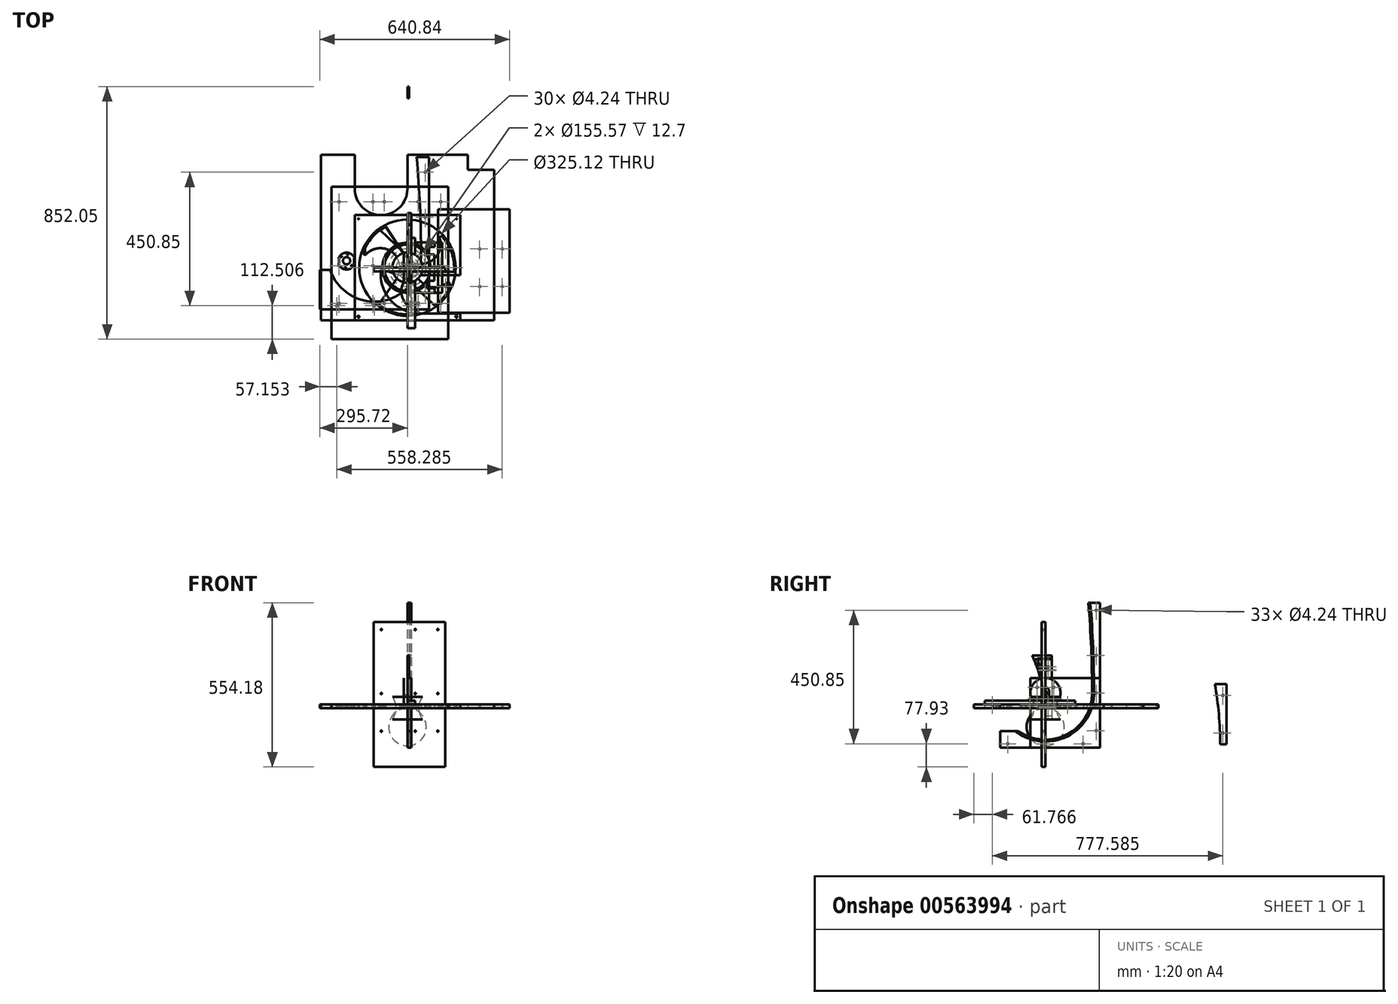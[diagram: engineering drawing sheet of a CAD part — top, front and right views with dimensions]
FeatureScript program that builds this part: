
annotation { "Feature Type Name" : "Feature", "Feature Type Description" : "" }
export const myFeature = defineFeature(function(context is Context, id is Id, definition is map)
    precondition{}
    {
        {
            var Q0;
            Q0=qCreatedBy(makeId("Front.planeOp"),FACE);
            var sketch = newSketch(context, id + "F0", { "sketchPlane" : qUnion([Q0])});
            skArc(sketch, "E0", {"start": v(50.8, 38.1) * mm, "mid": v(38.1, 0) * mm, "end": v(50.8, -38.1) * mm});
            skLineSegment(sketch, "E1.bottom", {"start": v(0, 38.1) * mm, "end": v(50.8, 38.1) * mm});
            skLineSegment(sketch, "E1.top", {"start": v(0, -38.1) * mm, "end": v(50.8, -38.1) * mm});
            skLineSegment(sketch, "E1.left", {"start": v(0, 38.1) * mm, "end": v(0, -38.1) * mm});
            skSolve(sketch);
        }
        {
            var Q0;
            Q0=qSketchRegion(id+"F0",true);
            var Q1;
            Q1=sQuery(id+"F0.wireOp",EDGE,"E1.left");
            revolve(context, id + "F1", {"entities" : qUnion([Q0]), "axis" : qUnion([Q1]), "revolveType" : RevolveType.FULL});
        }
        {
            var Q0;
            Q0=qCreatedBy(makeId("Right.planeOp"),FACE);
            var sketch = newSketch(context, id + "F2", { "sketchPlane" : qUnion([Q0])});
            skCircle(sketch, "E2", {"center": v(0, 50.8) * mm, "radius": 50.8 * mm});
            skCircle(sketch, "E3", {"center": v(0, 50.8) * mm, "radius": 6.35 * mm});
            skSolve(sketch);
        }
        {
            var Q0;
            Q0=qSketchRegion(id+"F2",true);
            extrude(context, id + "F3", {"entities" : qUnion([Q0]), "depth" : 25.4 * mm, "symmetric" : true});
        }
        {
            var Q0;
            Q0=qCreatedBy(makeId("Front.planeOp"),FACE);
            var sketch = newSketch(context, id + "F4", { "sketchPlane" : qUnion([Q0])});
            skArc(sketch, "E4", {"start": v(0, -127) * mm, "mid": v(63.5, -63.5) * mm, "end": v(0, 0) * mm});
            skLineSegment(sketch, "E5", {"start": v(0, 0) * mm, "end": v(0, -127) * mm});
            skSolve(sketch);
        }
        {
            var Q0;
            Q0=qSketchRegion(id+"F4",true);
            var Q1;
            Q1=sQuery(id+"F4.wireOp",EDGE,"E5");
            revolve(context, id + "F5", {"entities" : qUnion([Q0]), "axis" : qUnion([Q1]), "revolveType" : RevolveType.FULL});
        }
        {
            var Q0;
            Q0=qCreatedBy(makeId("Right.planeOp"),FACE);
            var sketch = newSketch(context, id + "F6", { "sketchPlane" : qUnion([Q0])});
            skLineSegment(sketch, "E6.top", {"start": v(-152.4, -133.35) * mm, "end": v(184.15, -133.35) * mm});
            skLineSegment(sketch, "E6.right", {"start": v(184.15, 50.8) * mm, "end": v(184.15, -133.35) * mm});
            skArc(sketch, "E7", {"start": v(-91.77, -77.18) * mm, "mid": v(71.93, -89.3) * mm, "end": v(157.48, 50.8) * mm});
            skLineSegment(sketch, "E8.left", {"start": v(184.15, 50.8) * mm, "end": v(184.15, 355.6) * mm});
            skArc(sketch, "E9", {"start": v(157.48, 50.8) * mm, "mid": v(154.4, 203.32) * mm, "end": v(145.19, 355.6) * mm});
            skCircle(sketch, "E10", {"center": v(-127, -120.65) * mm, "radius": 2.12 * mm});
            skCircle(sketch, "E11", {"center": v(0, -120.62) * mm, "radius": 2.12 * mm});
            skCircle(sketch, "E12", {"center": v(127, -120.62) * mm, "radius": 2.12 * mm});
            skCircle(sketch, "E13", {"center": v(171.45, 50.8) * mm, "radius": 2.12 * mm});
            skCircle(sketch, "E14", {"center": v(171.45, -76.2) * mm, "radius": 2.12 * mm});
            skCircle(sketch, "E15", {"center": v(171.45, 177.8) * mm, "radius": 2.12 * mm});
            skCircle(sketch, "E16", {"center": v(171.45, 330.2) * mm, "radius": 2.12 * mm});
            skLineSegment(sketch, "E17", {"start": v(-152.4, -77.18) * mm, "end": v(-91.77, -77.18) * mm});
            skLineSegment(sketch, "E18", {"start": v(-152.4, -77.18) * mm, "end": v(-152.4, -133.35) * mm});
            skPoint(sketch, "E19.orphan", {"position": v(-184.15, 0) * mm});
            skPoint(sketch, "E6.left.start.orphan", {"position": v(-184.15, -77.18) * mm});
            skPoint(sketch, "E20.orphan", {"position": v(-184.15, -133.35) * mm});
            skLineSegment(sketch, "E21", {"start": v(184.15, 355.6) * mm, "end": v(145.19, 355.6) * mm});
            skPoint(sketch, "E22.orphan", {"position": v(184.15, 381) * mm});
            skSolve(sketch);
        }
        {
            var Q0;
            Q0=qSketchRegion(id+"F6",true);
            extrude(context, id + "F7", {"entities" : qUnion([Q0]), "depth" : 12.7 * mm});
        }
        {
            var Q0;
            Q0=makeQuery(id+"F7.opExtrude","CAP_EDGE",EDGE,{"disambiguationData":[OSD([sQuery(id+"F6.wireOp",EDGE,"E9")])],"isStart":true});
            chamfer(context, id + "F8", {"entities" : qUnion([Q0]), "chamferType" : ChamferType.TWO_OFFSETS, "width1" : 3.66 * mm, "oppositeDirection" : false, "width2" : 6.35 * mm, "tangentPropagation" : true});
        }
        {
            var Q0;
            Q0=qCreatedBy(makeId("Top.planeOp"),FACE);
            var sketch = newSketch(context, id + "F9", { "sketchPlane" : qUnion([Q0])});
            skLineSegment(sketch, "E23.bottom", {"start": v(103.82, 196.85) * mm, "end": v(345.12, 196.85) * mm});
            skLineSegment(sketch, "E23.right", {"start": v(345.12, 196.85) * mm, "end": v(345.12, -152.4) * mm});
            skCircle(sketch, "E24", {"center": v(129.22, 63.5) * mm, "radius": 2.12 * mm});
            skCircle(sketch, "E25", {"center": v(129.22, -63.5) * mm, "radius": 2.12 * mm});
            skCircle(sketch, "E26", {"center": v(243.52, 63.5) * mm, "radius": 2.12 * mm});
            skCircle(sketch, "E27", {"center": v(243.52, -63.5) * mm, "radius": 2.12 * mm});
            skCircle(sketch, "E28", {"center": v(319.72, 63.5) * mm, "radius": 2.12 * mm});
            skCircle(sketch, "E29", {"center": v(319.72, -63.5) * mm, "radius": 2.12 * mm});
            skLineSegment(sketch, "E30", {"start": v(103.82, -152.4) * mm, "end": v(103.82, 196.85) * mm});
            skPoint(sketch, "E31.orphan", {"position": v(-48.58, 196.85) * mm});
            skPoint(sketch, "E32.center.orphan", {"position": v(-23.18, 63.5) * mm});
            skPoint(sketch, "E33.center.orphan", {"position": v(91.12, 63.5) * mm});
            skPoint(sketch, "E34.center.orphan", {"position": v(-23.18, -63.5) * mm});
            skPoint(sketch, "E35.center.orphan", {"position": v(91.12, -63.5) * mm});
            skLineSegment(sketch, "E36", {"start": v(103.82, -152.4) * mm, "end": v(345.12, -152.4) * mm});
            skPoint(sketch, "E23.top.start.orphan", {"position": v(103.82, -184.15) * mm});
            skSolve(sketch);
        }
        {
            var Q0;
            Q0=qSketchRegion(id+"F9",true);
            extrude(context, id + "F10", {"entities" : qUnion([Q0]), "depth" : 12.7 * mm});
        }
        {
            var Q0;
            Q0=qCreatedBy(makeId("Right.planeOp"),FACE);
            var sketch = newSketch(context, id + "F11", { "sketchPlane" : qUnion([Q0])});
            skLineSegment(sketch, "E37.bottom", {"start": v(-204.62, 25.4) * mm, "end": v(100.18, 25.4) * mm});
            skLineSegment(sketch, "E37.top", {"start": v(-204.62, 0) * mm, "end": v(100.18, 0) * mm});
            skLineSegment(sketch, "E37.left", {"start": v(-204.62, 25.4) * mm, "end": v(-204.62, 0) * mm});
            skLineSegment(sketch, "E37.right", {"start": v(100.18, 25.4) * mm, "end": v(100.18, 0) * mm});
            skCircle(sketch, "E38", {"center": v(-179.22, 12.7) * mm, "radius": 2.12 * mm});
            skCircle(sketch, "E39", {"center": v(-52.22, 12.7) * mm, "radius": 2.12 * mm});
            skCircle(sketch, "E40", {"center": v(74.78, 12.7) * mm, "radius": 2.12 * mm});
            skSolve(sketch);
        }
        {
            var Q0;
            Q0=qSketchRegion(id+"F11",true);
            extrude(context, id + "F12", {"entities" : qUnion([Q0]), "depth" : 25.4 * mm});
        }
        {
            var Q0;
            Q0=qCreatedBy(makeId("Top.planeOp"),FACE);
            var sketch = newSketch(context, id + "F13", { "sketchPlane" : qUnion([Q0])});
            skCircle(sketch, "E41", {"center": v(12.7, -115.72) * mm, "radius": 2.12 * mm});
            skCircle(sketch, "E42", {"center": v(12.7, 11.28) * mm, "radius": 2.12 * mm});
            skSolve(sketch);
        }
        {
            var Q0;
            Q0=sQuery(id+"F13.wireOp",VERTEX,"E41.center");
            var Q1;
            Q1=makeQuery(id+"F12.opExtrude","SWEPT_BODY",BODY,{"disambiguationData":[OSD([sQuery(id+"F11.wireOp",EDGE,"E37.bottom"),sQuery(id+"F11.wireOp",EDGE,"E37.top"),sQuery(id+"F11.wireOp",EDGE,"E37.left"),sQuery(id+"F11.wireOp",EDGE,"E37.right"),sQuery(id+"F11.wireOp",EDGE,"E38"),sQuery(id+"F11.wireOp",EDGE,"E39"),sQuery(id+"F11.wireOp",EDGE,"E40")])]});
            hole(context, id + "F14", {"style" : HoleStyle.SIMPLE, "endStyle" : HoleEndStyle.THROUGH, "oppositeDirection" : true, "holeDiameter" : 4.24 * mm, "isTappedThrough" : true, "tappedDepth" : 12.7 * mm, "tapClearance" : 3, "locations" : qUnion([Q0]), "scope" : qUnion([Q1]), "startStyle" : HoleStartStyle.PART});
        }
        {
            var Q0;
            Q0=sQuery(id+"F13.wireOp",VERTEX,"E42.center");
            var Q1;
            Q1=makeQuery(id+"F12.opExtrude","SWEPT_BODY",BODY,{"disambiguationData":[OSD([sQuery(id+"F11.wireOp",EDGE,"E37.bottom"),sQuery(id+"F11.wireOp",EDGE,"E37.top"),sQuery(id+"F11.wireOp",EDGE,"E37.left"),sQuery(id+"F11.wireOp",EDGE,"E37.right"),sQuery(id+"F11.wireOp",EDGE,"E38"),sQuery(id+"F11.wireOp",EDGE,"E39"),sQuery(id+"F11.wireOp",EDGE,"E40")])]});
            hole(context, id + "F15", {"style" : HoleStyle.SIMPLE, "endStyle" : HoleEndStyle.THROUGH, "oppositeDirection" : true, "holeDiameter" : 4.24 * mm, "isTappedThrough" : true, "tappedDepth" : 12.7 * mm, "tapClearance" : 3, "locations" : qUnion([Q0]), "scope" : qUnion([Q1]), "startStyle" : HoleStartStyle.PART});
        }
        {
            var Q0;
            Q0=qCreatedBy(makeId("Front.planeOp"),FACE);
            var sketch = newSketch(context, id + "F16", { "sketchPlane" : qUnion([Q0])});
            skLineSegment(sketch, "E43.top", {"start": v(-113.71, -198.58) * mm, "end": v(127.59, -198.58) * mm});
            skLineSegment(sketch, "E43.right", {"start": v(127.59, 290.37) * mm, "end": v(127.59, -198.58) * mm});
            skCircle(sketch, "E44", {"center": v(-88.31, 49.07) * mm, "radius": 2.12 * mm});
            skCircle(sketch, "E45", {"center": v(-88.31, -77.93) * mm, "radius": 2.12 * mm});
            skCircle(sketch, "E46", {"center": v(25.99, 49.07) * mm, "radius": 2.12 * mm});
            skCircle(sketch, "E47", {"center": v(25.99, -77.93) * mm, "radius": 2.12 * mm});
            skCircle(sketch, "E48", {"center": v(102.19, 49.07) * mm, "radius": 2.12 * mm});
            skCircle(sketch, "E49", {"center": v(102.19, -77.93) * mm, "radius": 2.12 * mm});
            skCircle(sketch, "E50", {"center": v(-88.31, 264.97) * mm, "radius": 2.12 * mm});
            skCircle(sketch, "E51", {"center": v(25.99, 264.97) * mm, "radius": 2.12 * mm});
            skCircle(sketch, "E52", {"center": v(102.19, 264.97) * mm, "radius": 2.12 * mm});
            skLineSegment(sketch, "E53", {"start": v(-113.71, 290.37) * mm, "end": v(-113.71, -198.58) * mm});
            skPoint(sketch, "E43.left.start.orphan", {"position": v(-266.11, 315.77) * mm});
            skPoint(sketch, "E54.center.orphan", {"position": v(-240.71, -77.93) * mm});
            skPoint(sketch, "E55.center.orphan", {"position": v(-126.41, -77.93) * mm});
            skPoint(sketch, "E56.center.orphan", {"position": v(-126.41, 49.07) * mm});
            skPoint(sketch, "E57.center.orphan", {"position": v(-240.71, 49.07) * mm});
            skPoint(sketch, "E58.center.orphan", {"position": v(-240.71, 264.97) * mm});
            skPoint(sketch, "E59.center.orphan", {"position": v(-126.41, 264.97) * mm});
            skLineSegment(sketch, "E60", {"start": v(-113.71, 290.37) * mm, "end": v(127.59, 290.37) * mm});
            skPoint(sketch, "E43.bottom.start.orphan", {"position": v(-113.71, 315.77) * mm});
            skSolve(sketch);
        }
        {
            var Q0;
            Q0=qSketchRegion(id+"F16",true);
            extrude(context, id + "F17", {"entities" : qUnion([Q0]), "depth" : 12.7 * mm});
        }
        {
            var Q0;
            Q0=qCreatedBy(makeId("Right.planeOp"),FACE);
            var sketch = newSketch(context, id + "F18", { "sketchPlane" : qUnion([Q0])});
            skLineSegment(sketch, "E61.bottom", {"start": v(184.15, -133.35) * mm, "end": v(-50.8, -133.35) * mm});
            skLineSegment(sketch, "E61.top", {"start": v(184.15, 101.6) * mm, "end": v(-50.8, 101.6) * mm});
            skLineSegment(sketch, "E61.left", {"start": v(184.15, -133.35) * mm, "end": v(184.15, 101.6) * mm});
            skLineSegment(sketch, "E61.right", {"start": v(-50.8, -133.35) * mm, "end": v(-50.8, 101.6) * mm});
            skCircle(sketch, "E62", {"center": v(171.45, 50.8) * mm, "radius": 2.12 * mm});
            skCircle(sketch, "E63", {"center": v(171.45, -76.2) * mm, "radius": 2.12 * mm});
            skCircle(sketch, "E64", {"center": v(127, -120.62) * mm, "radius": 2.12 * mm});
            skCircle(sketch, "E65", {"center": v(0, -120.62) * mm, "radius": 2.12 * mm});
            skArc(sketch, "E66", {"start": v(12.7, 57.15) * mm, "mid": v(0, 69.85) * mm, "end": v(-12.7, 57.15) * mm});
            skArc(sketch, "E67", {"start": v(-12.7, 44.45) * mm, "mid": v(0, 31.75) * mm, "end": v(12.7, 44.45) * mm});
            skLineSegment(sketch, "E68", {"start": v(-12.7, 44.45) * mm, "end": v(-12.7, 57.15) * mm});
            skLineSegment(sketch, "E69", {"start": v(12.7, 57.15) * mm, "end": v(12.7, 44.45) * mm});
            skCircle(sketch, "E70", {"center": v(27.94, 69.85) * mm, "radius": 2.12 * mm});
            skPoint(sketch, "E70.centerSnap0", {"position": v(0, 69.85) * mm});
            skCircle(sketch, "E71", {"center": v(-27.94, 69.85) * mm, "radius": 2.12 * mm});
            skCircle(sketch, "E72", {"center": v(27.94, 31.75) * mm, "radius": 2.12 * mm});
            skPoint(sketch, "E72.centerSnap0", {"position": v(0, 31.75) * mm});
            skCircle(sketch, "E73", {"center": v(-27.94, 31.75) * mm, "radius": 2.12 * mm});
            skSolve(sketch);
        }
        {
            var Q0;
            Q0=qSketchRegion(id+"F18",true);
            extrude(context, id + "F19", {"entities" : qUnion([Q0]), "depth" : 12.7 * mm});
        }
        {
            var Q0;
            Q0=qSketchRegion(id+"F6",true);
            extrude(context, id + "F20", {"entities" : qUnion([Q0]), "depth" : 12.7 * mm});
        }
        {
            var Q0;
            Q0=makeQuery(id+"F20.opExtrude","CAP_EDGE",EDGE,{"disambiguationData":[OSD([sQuery(id+"F6.wireOp",EDGE,"E9")])],"isStart":false});
            chamfer(context, id + "F21", {"entities" : qUnion([Q0]), "chamferType" : ChamferType.TWO_OFFSETS, "width1" : 6.35 * mm, "oppositeDirection" : false, "width2" : 3.66 * mm, "tangentPropagation" : true});
        }
        {
            var Q0;
            Q0=qCreatedBy(makeId("Top.planeOp"),FACE);
            var sketch = newSketch(context, id + "F22", { "sketchPlane" : qUnion([Q0])});
            skLineSegment(sketch, "E74.top", {"start": v(-295.72, -141.18) * mm, "end": v(72.58, -141.18) * mm});
            skLineSegment(sketch, "E74.left", {"start": v(-295.72, -7.83) * mm, "end": v(-295.72, -141.18) * mm});
            skLineSegment(sketch, "E74.right", {"start": v(72.58, 42.97) * mm, "end": v(72.58, -141.18) * mm});
            skArc(sketch, "E75", {"start": v(-260.63, -7.83) * mm, "mid": v(-85.82, -112.4) * mm, "end": v(45.91, 42.97) * mm});
            skLineSegment(sketch, "E76.top", {"start": v(72.58, 373.17) * mm, "end": v(31.48, 373.17) * mm});
            skLineSegment(sketch, "E76.left", {"start": v(72.58, 42.97) * mm, "end": v(72.58, 373.17) * mm});
            skArc(sketch, "E77", {"start": v(45.91, 42.97) * mm, "mid": v(42.3, 208.22) * mm, "end": v(31.48, 373.17) * mm});
            skCircle(sketch, "E78", {"center": v(-238.57, -128.48) * mm, "radius": 2.12 * mm});
            skCircle(sketch, "E79", {"center": v(-111.57, -128.46) * mm, "radius": 2.12 * mm});
            skCircle(sketch, "E80", {"center": v(15.43, -128.46) * mm, "radius": 2.12 * mm});
            skCircle(sketch, "E81", {"center": v(59.88, 42.97) * mm, "radius": 2.12 * mm});
            skCircle(sketch, "E82", {"center": v(59.88, -84.03) * mm, "radius": 2.12 * mm});
            skCircle(sketch, "E83", {"center": v(59.88, 169.97) * mm, "radius": 2.12 * mm});
            skCircle(sketch, "E84", {"center": v(59.88, 322.37) * mm, "radius": 2.12 * mm});
            skLineSegment(sketch, "E85", {"start": v(-295.72, -7.83) * mm, "end": v(-260.63, -7.83) * mm});
            skSolve(sketch);
        }
        {
            var Q0;
            Q0=qSketchRegion(id+"F22",true);
            extrude(context, id + "F23", {"entities" : qUnion([Q0]), "depth" : 12.7 * mm});
        }
        {
            var Q0;
            Q0=qCreatedBy(makeId("Top.planeOp"),FACE);
            var sketch = newSketch(context, id + "F24", { "sketchPlane" : qUnion([Q0])});
            skLineSegment(sketch, "E86.bottom", {"start": v(-256.02, 273.36) * mm, "end": v(137.68, 273.36) * mm});
            skLineSegment(sketch, "E86.top", {"start": v(-256.02, -241) * mm, "end": v(137.68, -241) * mm});
            skLineSegment(sketch, "E86.left", {"start": v(-256.02, 273.36) * mm, "end": v(-256.02, -241) * mm});
            skLineSegment(sketch, "E86.right", {"start": v(137.68, 273.36) * mm, "end": v(137.68, -241) * mm});
            skCircle(sketch, "E87", {"center": v(-230.62, -120.34) * mm, "radius": 2.12 * mm});
            skCircle(sketch, "E88", {"center": v(-230.62, 6.66) * mm, "radius": 2.12 * mm});
            skCircle(sketch, "E89", {"center": v(-116.32, 6.66) * mm, "radius": 2.12 * mm});
            skCircle(sketch, "E90", {"center": v(-116.32, -120.34) * mm, "radius": 2.12 * mm});
            skCircle(sketch, "E91", {"center": v(-78.22, 6.66) * mm, "radius": 2.12 * mm});
            skCircle(sketch, "E92", {"center": v(-78.22, -120.34) * mm, "radius": 2.12 * mm});
            skCircle(sketch, "E93", {"center": v(36.08, 6.66) * mm, "radius": 2.12 * mm});
            skCircle(sketch, "E94", {"center": v(36.08, -120.34) * mm, "radius": 2.12 * mm});
            skCircle(sketch, "E95", {"center": v(112.28, 6.66) * mm, "radius": 2.12 * mm});
            skCircle(sketch, "E96", {"center": v(112.28, -120.34) * mm, "radius": 2.12 * mm});
            skCircle(sketch, "E97", {"center": v(-230.62, 222.56) * mm, "radius": 2.12 * mm});
            skCircle(sketch, "E98", {"center": v(-116.32, 222.56) * mm, "radius": 2.12 * mm});
            skCircle(sketch, "E99", {"center": v(-78.22, 222.56) * mm, "radius": 2.12 * mm});
            skCircle(sketch, "E100", {"center": v(36.08, 222.56) * mm, "radius": 2.12 * mm});
            skCircle(sketch, "E101", {"center": v(112.28, 222.56) * mm, "radius": 2.12 * mm});
            skSolve(sketch);
        }
        {
            var Q0;
            Q0=qSketchRegion(id+"F24",true);
            extrude(context, id + "F25", {"entities" : qUnion([Q0]), "depth" : 12.7 * mm});
        }
        {
            var Q0;
            Q0=qCreatedBy(makeId("Right.planeOp"),FACE);
            var sketch = newSketch(context, id + "F26", { "sketchPlane" : qUnion([Q0])});
            skLineSegment(sketch, "E102.right", {"start": v(21.59, 12.7) * mm, "end": v(21.59, -25.4) * mm});
            skLineSegment(sketch, "E103.left", {"start": v(21.59, 12.7) * mm, "end": v(21.59, 177.8) * mm});
            skCircle(sketch, "E104", {"center": v(8.9, 12.7) * mm, "radius": 2.12 * mm});
            skCircle(sketch, "E105", {"center": v(8.89, 139.7) * mm, "radius": 2.12 * mm});
            skPoint(sketch, "E106", {"position": v(0, -25.4) * mm});
            skArc(sketch, "E107", {"start": v(0, -25.4) * mm, "mid": v(-11.35, 78.65) * mm, "end": v(-44.86, 177.8) * mm});
            skLineSegment(sketch, "E108", {"start": v(0, -25.4) * mm, "end": v(21.59, -25.4) * mm});
            skLineSegment(sketch, "E109", {"start": v(21.59, 177.8) * mm, "end": v(-44.86, 177.8) * mm});
            skPoint(sketch, "E110.center.orphan", {"position": v(-3897.8, 104.27) * mm});
            skSolve(sketch);
        }
        {
            var Q0;
            Q0=qSketchRegion(id+"F26",true);
            extrude(context, id + "F27", {"entities" : qUnion([Q0]), "depth" : 5.08 * mm});
        }
        {
            var Q0;
            Q0=qCreatedBy(makeId("Right.planeOp"),FACE);
            var sketch = newSketch(context, id + "F28", { "sketchPlane" : qUnion([Q0])});
            skLineSegment(sketch, "E111.right", {"start": v(21.59, 0.17) * mm, "end": v(21.59, -37.93) * mm});
            skLineSegment(sketch, "E112.left", {"start": v(21.59, 0.17) * mm, "end": v(21.59, 165.27) * mm});
            skCircle(sketch, "E113", {"center": v(8.9, 0.17) * mm, "radius": 2.12 * mm});
            skCircle(sketch, "E114", {"center": v(8.9, 127.17) * mm, "radius": 2.12 * mm});
            skPoint(sketch, "E115", {"position": v(0, -37.93) * mm});
            skLineSegment(sketch, "E116", {"start": v(0, -37.93) * mm, "end": v(21.59, -37.93) * mm});
            skLineSegment(sketch, "E117", {"start": v(21.59, 165.27) * mm, "end": v(-36.48, 165.27) * mm});
            skPoint(sketch, "E118.center.orphan", {"position": v(-3452.32, 0.17) * mm});
            skArc(sketch, "E119", {"start": v(0, -37.93) * mm, "mid": v(-9.2, 65.3) * mm, "end": v(-36.48, 165.27) * mm});
            skPoint(sketch, "E120.center.orphan", {"position": v(-482.6, -37.93) * mm});
            skSolve(sketch);
        }
        {
            var Q0;
            Q0=qSketchRegion(id+"F28",true);
            extrude(context, id + "F29", {"entities" : qUnion([Q0]), "depth" : 5.08 * mm});
        }
        {
            var Q0;
            Q0=qCreatedBy(makeId("Right.planeOp"),FACE);
            var sketch = newSketch(context, id + "F30", { "sketchPlane" : qUnion([Q0])});
            skLineSegment(sketch, "E121.right", {"start": v(21.59, 2.25) * mm, "end": v(21.59, -35.85) * mm});
            skLineSegment(sketch, "E122.left", {"start": v(21.59, 2.25) * mm, "end": v(21.59, 167.35) * mm});
            skCircle(sketch, "E123", {"center": v(8.9, 2.25) * mm, "radius": 2.12 * mm});
            skCircle(sketch, "E124", {"center": v(8.9, 129.25) * mm, "radius": 2.12 * mm});
            skPoint(sketch, "E125", {"position": v(0, -35.85) * mm});
            skLineSegment(sketch, "E126", {"start": v(0, -35.85) * mm, "end": v(21.59, -35.85) * mm});
            skLineSegment(sketch, "E127", {"start": v(21.59, 167.35) * mm, "end": v(-26.67, 167.35) * mm});
            skPoint(sketch, "E128.center.orphan", {"position": v(-3488.51, 2.25) * mm});
            skArc(sketch, "E129", {"start": v(0, -35.85) * mm, "mid": v(-6.7, 66.62) * mm, "end": v(-26.67, 167.35) * mm});
            skPoint(sketch, "E130.center.orphan", {"position": v(-482.6, -35.85) * mm});
            skSolve(sketch);
        }
        {
            var Q0;
            Q0=qSketchRegion(id+"F30",true);
            extrude(context, id + "F31", {"entities" : qUnion([Q0]), "depth" : 5.08 * mm});
        }
        {
            var Q0;
            Q0=qCreatedBy(makeId("Right.planeOp"),FACE);
            var sketch = newSketch(context, id + "F32", { "sketchPlane" : qUnion([Q0])});
            skLineSegment(sketch, "E131.right", {"start": v(611.06, -84.17) * mm, "end": v(611.06, -122.27) * mm});
            skLineSegment(sketch, "E132.left", {"start": v(611.06, -84.17) * mm, "end": v(611.06, 80.93) * mm});
            skCircle(sketch, "E133", {"center": v(598.36, -84.17) * mm, "radius": 2.12 * mm});
            skCircle(sketch, "E134", {"center": v(598.36, 42.83) * mm, "radius": 2.12 * mm});
            skPoint(sketch, "E135", {"position": v(589.47, -122.27) * mm});
            skLineSegment(sketch, "E136", {"start": v(589.47, -122.27) * mm, "end": v(611.06, -122.27) * mm});
            skLineSegment(sketch, "E137", {"start": v(611.06, 80.93) * mm, "end": v(571.67, 80.93) * mm});
            skPoint(sketch, "E138.center.orphan", {"position": v(-3200.2, -84.17) * mm});
            skArc(sketch, "E139", {"start": v(589.47, -122.27) * mm, "mid": v(585.01, -20.28) * mm, "end": v(571.67, 80.93) * mm});
            skPoint(sketch, "E140.center.orphan", {"position": v(106.87, -122.27) * mm});
            skSolve(sketch);
        }
        {
            var Q0;
            Q0=qSketchRegion(id+"F32",true);
            extrude(context, id + "F33", {"entities" : qUnion([Q0]), "depth" : 5.08 * mm});
        }
        {
            var Q0;
            Q0=qCreatedBy(makeId("Top.planeOp"),FACE);
            var sketch = newSketch(context, id + "F34", { "sketchPlane" : qUnion([Q0])});
            skCircle(sketch, "E141", {"center": v(0, 0) * mm, "radius": 77.79 * mm});
            skArc(sketch, "E142", {"start": v(71.44, 44.45) * mm, "mid": v(-84.14, 0) * mm, "end": v(71.44, -44.45) * mm});
            skLineSegment(sketch, "E143.bottom", {"start": v(90.62, 44.45) * mm, "end": v(77.92, 44.45) * mm});
            skLineSegment(sketch, "E143.top", {"start": v(90.62, -44.45) * mm, "end": v(77.92, -44.45) * mm});
            skLineSegment(sketch, "E143.left", {"start": v(90.62, 44.45) * mm, "end": v(90.62, -44.45) * mm});
            skLineSegment(sketch, "E144", {"start": v(77.92, 44.45) * mm, "end": v(71.44, 44.45) * mm});
            skLineSegment(sketch, "E145", {"start": v(77.92, -44.45) * mm, "end": v(71.44, -44.45) * mm});
            skSolve(sketch);
        }
        {
            var Q0;
            Q0=makeQuery(id+"F34.imprint","IMPRINT",FACE,{"disambiguationData":[TD([[makeQuery(id+"F34.imprint","IMPRINT",EDGE,{"derivedFrom":sQuery(id+"F34.wireOp",EDGE,"E141")}),-1.0]])]});
            extrude(context, id + "F35", {"entities" : qUnion([Q0]), "depth" : 12.7 * mm});
        }
        {
            var Q0;
            Q0=qCreatedBy(makeId("Top.planeOp"),FACE);
            var sketch = newSketch(context, id + "F36", { "sketchPlane" : qUnion([Q0])});
            skArc(sketch, "E146", {"start": v(64.77, 43.08) * mm, "mid": v(-77.79, 0) * mm, "end": v(64.77, -43.08) * mm});
            skArc(sketch, "E147", {"start": v(0, 85.1) * mm, "mid": v(-85.1, 0) * mm, "end": v(0, -85.1) * mm});
            skLineSegment(sketch, "E148.bottom", {"start": v(0, 85.1) * mm, "end": v(91.44, 85.1) * mm});
            skLineSegment(sketch, "E148.top", {"start": v(64.77, 69.85) * mm, "end": v(91.44, 69.85) * mm});
            skLineSegment(sketch, "E148.right", {"start": v(91.44, 85.1) * mm, "end": v(91.44, 69.85) * mm});
            skLineSegment(sketch, "E149", {"start": v(64.77, 69.85) * mm, "end": v(64.77, 55.18) * mm});
            skLineSegment(sketch, "E150.bottom", {"start": v(0, -85.1) * mm, "end": v(91.44, -85.1) * mm});
            skLineSegment(sketch, "E150.top", {"start": v(64.77, -69.85) * mm, "end": v(91.44, -69.85) * mm});
            skLineSegment(sketch, "E150.right", {"start": v(91.44, -85.1) * mm, "end": v(91.44, -69.85) * mm});
            skLineSegment(sketch, "E151", {"start": v(64.77, -69.85) * mm, "end": v(64.77, -43.08) * mm});
            skLineSegment(sketch, "E152.trimOffspring", {"start": v(64.77, 43.08) * mm, "end": v(64.77, 55.18) * mm});
            skPoint(sketch, "E153.orphan", {"position": v(0, -69.85) * mm});
            skSolve(sketch);
        }
        {
            var Q0;
            Q0=qSketchRegion(id+"F36",true);
            extrude(context, id + "F37", {"entities" : qUnion([Q0]), "depth" : 12.7 * mm});
        }
        {
            var Q0;
            Q0=qCreatedBy(makeId("Top.planeOp"),FACE);
            var sketch = newSketch(context, id + "F38", { "sketchPlane" : qUnion([Q0])});
            skArc(sketch, "E154", {"start": v(-37.12, -37.56) * mm, "mid": v(-49.9, 51.34) * mm, "end": v(-139.5, 45.28) * mm});
            skArc(sketch, "E155", {"start": v(-10.26, 44.15) * mm, "mid": v(73.55, 19.3) * mm, "end": v(108.6, 99.4) * mm});
            skArc(sketch, "E156", {"start": v(44.3, -13.16) * mm, "mid": v(-20.04, -73.08) * mm, "end": v(32.15, -143.82) * mm});
            skArc(sketch, "E157", {"start": v(-96.9, -124.15) * mm, "mid": v(-35.87, -153.34) * mm, "end": v(31.77, -154.24) * mm});
            skLineSegment(sketch, "E158", {"start": v(44.3, -13.16) * mm, "end": v(156.93, -13.16) * mm});
            skLineSegment(sketch, "E159", {"start": v(-10.26, 44.15) * mm, "end": v(-73.77, 139.13) * mm});
            skLineSegment(sketch, "E160", {"start": v(-37.06, -37.47) * mm, "end": v(-96.9, -124.15) * mm});
            skArc(sketch, "E161.trimOffspring", {"start": v(156.93, -13.16) * mm, "mid": v(149.66, 49) * mm, "end": v(118.76, 103.42) * mm});
            skArc(sketch, "E162.trimOffspring", {"start": v(-73.77, 139.13) * mm, "mid": v(-119.51, 102.55) * mm, "end": v(-148.72, 51.79) * mm});
            skArc(sketch, "E163", {"start": v(118.76, 103.42) * mm, "mid": v(112.13, 105.3) * mm, "end": v(108.6, 99.4) * mm});
            skArc(sketch, "E164", {"start": v(31.45, -154.3) * mm, "mid": v(35.93, -148.85) * mm, "end": v(31.19, -143.61) * mm});
            skArc(sketch, "E165", {"start": v(-148.72, 51.79) * mm, "mid": v(-146.66, 44.93) * mm, "end": v(-139.5, 45.28) * mm});
            skPoint(sketch, "E166.start.orphan", {"position": v(-148.72, 51.37) * mm});
            skCircle(sketch, "E167", {"center": v(0, 0) * mm, "radius": 12.2 * mm});
            skArc(sketch, "E168", {"start": v(-9.64, 21.78) * mm, "mid": v(-11.9, 20.62) * mm, "end": v(-14.03, 19.24) * mm});
            skCircle(sketch, "E169", {"center": v(23.81, 0) * mm, "radius": 2.54 * mm});
            skCircle(sketch, "E170", {"center": v(-11.9, 20.62) * mm, "radius": 2.54 * mm});
            skCircle(sketch, "E171", {"center": v(-11.9, -20.62) * mm, "radius": 2.54 * mm});
            skArc(sketch, "E172.trimOffspring", {"start": v(-14.03, -19.24) * mm, "mid": v(-11.9, -20.62) * mm, "end": v(-9.64, -21.78) * mm});
            skArc(sketch, "E173.trimOffspring", {"start": v(23.68, -2.54) * mm, "mid": v(23.81, 0) * mm, "end": v(23.68, 2.54) * mm});
            skSolve(sketch);
        }
        {
            var Q0;
            Q0=qSketchRegion(id+"F38",true);
            extrude(context, id + "F39", {"entities" : qUnion([Q0]), "depth" : 12.7 * mm, "offsetDistance" : 25.4 * mm});
        }
        {
            var Q0;
            Q0=qCreatedBy(makeId("Top.planeOp"),FACE);
            var sketch = newSketch(context, id + "F40", { "sketchPlane" : qUnion([Q0])});
            skLineSegment(sketch, "E174.bottom", {"start": v(-292.1, 381) * mm, "end": v(-177.8, 381) * mm});
            skLineSegment(sketch, "E174.top", {"start": v(-292.1, -177.8) * mm, "end": v(292.1, -177.8) * mm});
            skLineSegment(sketch, "E174.left", {"start": v(-292.1, 381) * mm, "end": v(-292.1, -177.8) * mm});
            skLineSegment(sketch, "E174.right", {"start": v(292.1, 330.2) * mm, "end": v(292.1, -177.8) * mm});
            skCircle(sketch, "E175", {"center": v(0, 0) * mm, "radius": 162.56 * mm});
            skCircle(sketch, "E176", {"center": v(-165.1, -165.1) * mm, "radius": 3.18 * mm});
            skCircle(sketch, "E177", {"center": v(165.1, -165.1) * mm, "radius": 3.18 * mm});
            skArc(sketch, "E178", {"start": v(-177.8, 266.7) * mm, "mid": v(-88.9, 177.8) * mm, "end": v(0, 266.7) * mm});
            skLineSegment(sketch, "E179", {"start": v(-177.8, 266.7) * mm, "end": v(-177.8, 381) * mm});
            skLineSegment(sketch, "E180", {"start": v(0, 266.7) * mm, "end": v(0, 381) * mm});
            skLineSegment(sketch, "E181.trimOffspring", {"start": v(0, 381) * mm, "end": v(203.2, 381) * mm});
            skLineSegment(sketch, "E182", {"start": v(203.2, 381) * mm, "end": v(203.2, 330.2) * mm});
            skLineSegment(sketch, "E183", {"start": v(203.2, 330.2) * mm, "end": v(292.1, 330.2) * mm});
            skPoint(sketch, "E184.orphan", {"position": v(292.1, 381) * mm});
            skSolve(sketch);
        }
        {
            var Q0;
            Q0=qSketchRegion(id+"F40",true);
            extrude(context, id + "F41", {"entities" : qUnion([Q0]), "depth" : 12.7 * mm, "offsetDistance" : 25.4 * mm});
        }
        {
            var Q0;
            Q0=qCreatedBy(makeId("Top.planeOp"),FACE);
            var sketch = newSketch(context, id + "F42", { "sketchPlane" : qUnion([Q0])});
            skLineSegment(sketch, "E185.bottom", {"start": v(-177.8, 177.8) * mm, "end": v(177.8, 177.8) * mm});
            skLineSegment(sketch, "E185.top", {"start": v(-177.8, -177.8) * mm, "end": v(177.8, -177.8) * mm});
            skLineSegment(sketch, "E185.left", {"start": v(-177.8, 177.8) * mm, "end": v(-177.8, -177.8) * mm});
            skLineSegment(sketch, "E185.right", {"start": v(177.8, 177.8) * mm, "end": v(177.8, -25.4) * mm});
            skCircle(sketch, "E186", {"center": v(-165.1, -165.1) * mm, "radius": 1.63 * mm});
            skCircle(sketch, "E187", {"center": v(165.1, -165.1) * mm, "radius": 1.63 * mm});
            skCircle(sketch, "E188", {"center": v(165.1, 165.1) * mm, "radius": 1.63 * mm});
            skCircle(sketch, "E189", {"center": v(-165.1, 165.1) * mm, "radius": 1.63 * mm});
            skLineSegment(sketch, "E190", {"start": v(0, -25.4) * mm, "end": v(177.8, -25.4) * mm});
            skLineSegment(sketch, "E191", {"start": v(31.43, -154.94) * mm, "end": v(177.8, -154.94) * mm});
            skArc(sketch, "E192", {"start": v(-88.9, 0) * mm, "mid": v(-46.23, -18.93) * mm, "end": v(0, -25.4) * mm});
            skArc(sketch, "E193", {"start": v(-88.9, 0) * mm, "mid": v(-61.88, -103.21) * mm, "end": v(31.43, -154.94) * mm});
            skPoint(sketch, "E194.end.orphan", {"position": v(177.8, -88.9) * mm});
            skPoint(sketch, "E194.start.orphan", {"position": v(0, -88.9) * mm});
            skPoint(sketch, "E195.orphan", {"position": v(0, -154.94) * mm});
            skCircle(sketch, "E196", {"center": v(0, 0) * mm, "radius": 22.25 * mm});
            skLineSegment(sketch, "E197.trimOffspring", {"start": v(177.8, -154.94) * mm, "end": v(177.8, -177.8) * mm});
            skSolve(sketch);
        }
        {
            var Q0;
            Q0=qSketchRegion(id+"F42",true);
            extrude(context, id + "F43", {"entities" : qUnion([Q0]), "depth" : 12.7 * mm, "offsetDistance" : 25.4 * mm});
        }
        {
            var Q0;
            Q0=qCreatedBy(makeId("Top.planeOp"),FACE);
            var sketch = newSketch(context, id + "F44", { "sketchPlane" : qUnion([Q0])});
            skArc(sketch, "E198", {"start": v(-92.16, 127.7) * mm, "mid": v(-120.86, 100.97) * mm, "end": v(-142.05, 67.98) * mm});
            skArc(sketch, "E199", {"start": v(-26.34, -11.09) * mm, "mid": v(-61.12, 58.67) * mm, "end": v(-138.14, 46.7) * mm});
            skArc(sketch, "E200", {"start": v(26.34, 11.09) * mm, "mid": v(61.12, -58.67) * mm, "end": v(138.14, -46.7) * mm});
            skCircle(sketch, "E201", {"center": v(-18.24, 15.3) * mm, "radius": 2.54 * mm});
            skCircle(sketch, "E202", {"center": v(4.13, 23.45) * mm, "radius": 2.54 * mm});
            skCircle(sketch, "E203", {"center": v(18.24, -15.3) * mm, "radius": 2.54 * mm});
            skCircle(sketch, "E204", {"center": v(-4.13, -23.45) * mm, "radius": 2.54 * mm});
            skArc(sketch, "E205", {"start": v(-26.34, -11.09) * mm, "mid": v(-23.54, -16.2) * mm, "end": v(-19.76, -20.64) * mm});
            skLineSegment(sketch, "E206", {"start": v(-19.76, -20.64) * mm, "end": v(92.08, -127.75) * mm});
            skLineSegment(sketch, "E207", {"start": v(17.99, 22.2) * mm, "end": v(-92.16, 127.7) * mm});
            skArc(sketch, "E208", {"start": v(-138.14, 46.7) * mm, "mid": v(-143.4, 56.73) * mm, "end": v(-142.05, 67.98) * mm});
            skArc(sketch, "E209", {"start": v(138.14, -46.7) * mm, "mid": v(143.25, -55.82) * mm, "end": v(142.85, -66.28) * mm});
            skArc(sketch, "E210.trimOffspring", {"start": v(26.34, 11.09) * mm, "mid": v(22.85, 17.16) * mm, "end": v(17.99, 22.2) * mm});
            skArc(sketch, "E211.trimOffspring", {"start": v(92.08, -127.75) * mm, "mid": v(121.42, -100.28) * mm, "end": v(142.85, -66.28) * mm});
            skCircle(sketch, "E212", {"center": v(0.17, 0.98) * mm, "radius": 12.2 * mm});
            skSolve(sketch);
        }
        {
            var Q0;
            Q0=qSketchRegion(id+"F44",true);
            extrude(context, id + "F45", {"entities" : qUnion([Q0]), "depth" : 12.7 * mm, "offsetDistance" : 25.4 * mm});
        }
        {
            var Q0;
            Q0=qCreatedBy(makeId("Top.planeOp"),FACE);
            var sketch = newSketch(context, id + "F46", { "sketchPlane" : qUnion([Q0])});
            skArc(sketch, "E213", {"start": v(-231.82, 11.37) * mm, "mid": v(-230.88, 22.46) * mm, "end": v(-231.82, 33.54) * mm});
            skArc(sketch, "E214", {"start": v(-179.15, 33.54) * mm, "mid": v(-180.08, 22.46) * mm, "end": v(-179.15, 11.37) * mm});
            skCircle(sketch, "E215", {"center": v(-223.72, 37.77) * mm, "radius": 2.54 * mm});
            skCircle(sketch, "E216", {"center": v(-201.35, 45.9) * mm, "radius": 2.54 * mm});
            skCircle(sketch, "E217", {"center": v(-187.24, 7.15) * mm, "radius": 2.54 * mm});
            skCircle(sketch, "E218", {"center": v(-209.62, -1) * mm, "radius": 2.54 * mm});
            skArc(sketch, "E219", {"start": v(-231.82, 11.37) * mm, "mid": v(-229.02, 6.26) * mm, "end": v(-225.25, 1.82) * mm});
            skArc(sketch, "E220.trimOffspring", {"start": v(-179.15, 33.54) * mm, "mid": v(-182.63, 39.62) * mm, "end": v(-187.5, 44.66) * mm});
            skCircle(sketch, "E221", {"center": v(-205.31, 23.43) * mm, "radius": 12.2 * mm});
            skArc(sketch, "E222", {"start": v(-231.82, 11.37) * mm, "mid": v(-205.48, -6.12) * mm, "end": v(-179.15, 11.37) * mm});
            skArc(sketch, "E223.trimOffspring", {"start": v(-179.15, 33.54) * mm, "mid": v(-205.48, 51.03) * mm, "end": v(-231.82, 33.54) * mm});
            skSolve(sketch);
        }
        {
            var Q0;
            {var subQ1=sQuery(id+"F46.wireOp",EDGE,"E213");Q0=makeQuery(id+"F46.imprint","IMPRINT",FACE,{"disambiguationData":[TD([[makeQuery(id+"F46.imprint","IMPRINT",EDGE,{"derivedFrom":subQ1}),-1.0]])]});}
            extrude(context, id + "F47", {"entities" : qUnion([Q0]), "depth" : 12.7 * mm, "offsetDistance" : 25.4 * mm});
        }
        {
            var Q0;
            Q0=qCreatedBy(makeId("Top.planeOp"),FACE);
            var sketch = newSketch(context, id + "F48", { "sketchPlane" : qUnion([Q0])});
            skArc(sketch, "E224", {"start": v(64.77, 43.08) * mm, "mid": v(-77.79, 0) * mm, "end": v(64.77, -43.08) * mm});
            skArc(sketch, "E225", {"start": v(0, 85.1) * mm, "mid": v(-85.1, 0) * mm, "end": v(0, -85.1) * mm});
            skLineSegment(sketch, "E226.bottom", {"start": v(0, 85.1) * mm, "end": v(116.84, 85.1) * mm});
            skLineSegment(sketch, "E226.right", {"start": v(116.84, 85.1) * mm, "end": v(116.84, 69.85) * mm});
            skLineSegment(sketch, "E227.bottom", {"start": v(0, -85.1) * mm, "end": v(116.84, -85.1) * mm});
            skLineSegment(sketch, "E227.right", {"start": v(116.84, -85.1) * mm, "end": v(116.84, -69.85) * mm});
            skPoint(sketch, "E228.orphan", {"position": v(-152.45, -69.85) * mm});
            skLineSegment(sketch, "E229", {"start": v(116.84, 69.85) * mm, "end": v(116.84, -69.85) * mm});
            skCircle(sketch, "E230", {"center": v(0, 0) * mm, "radius": 77.79 * mm});
            skPoint(sketch, "E231.start.orphan", {"position": v(90.17, 69.85) * mm});
            skPoint(sketch, "E232.trimOffspring.end.orphan", {"position": v(64.77, 55.18) * mm});
            skPoint(sketch, "E227.top.start.orphan", {"position": v(64.77, -69.85) * mm});
            skSolve(sketch);
        }
        {
            var Q0;
            Q0 = qSketchRegion(id + "F48", true);
            extrude(context, id + "F49", {"entities" : qUnion([Q0]), "depth" : 12.7 * mm, "offsetDistance" : 25.4 * mm});
        }
    });
